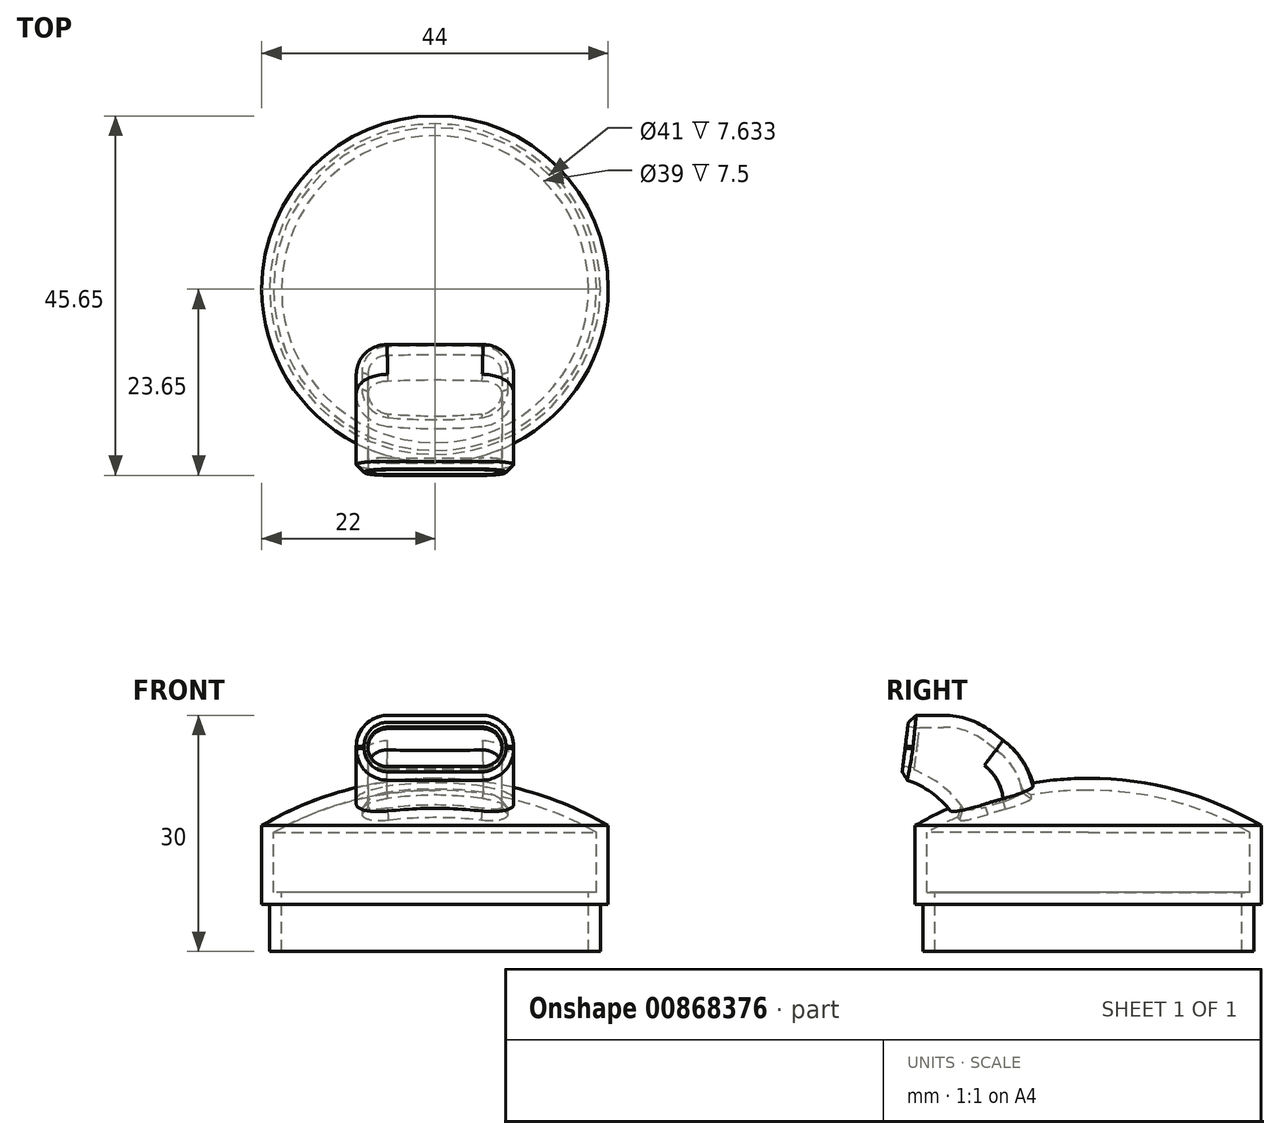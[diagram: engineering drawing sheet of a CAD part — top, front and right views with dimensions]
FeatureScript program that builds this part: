
annotation { "Feature Type Name" : "Feature", "Feature Type Description" : "" }
export const myFeature = defineFeature(function(context is Context, id is Id, definition is map)
    precondition{}
    {
        {
            var Q0;
            Q0=qCreatedBy(makeId("Front.planeOp"),FACE);
            var sketch = newSketch(context, id + "F0", { "sketchPlane" : qUnion([Q0])});
            skLineSegment(sketch, "E0", {"start": v(0, 0) * mm, "end": v(-21, 0) * mm});
            skLineSegment(sketch, "E1", {"start": v(-21, 0) * mm, "end": v(-21, 6) * mm});
            skLineSegment(sketch, "E2", {"start": v(-21, 6) * mm, "end": v(-22, 6) * mm});
            skLineSegment(sketch, "E3", {"start": v(-22, 6) * mm, "end": v(-22, 16) * mm});
            skLineSegment(sketch, "E4", {"start": v(0, 22) * mm, "end": v(0, 0) * mm});
            skArc(sketch, "E5", {"start": v(0, 22) * mm, "mid": v(-11.4, 20.47) * mm, "end": v(-22, 16) * mm});
            skSolve(sketch);
        }
        {
            var Q0;
            Q0 = qSketchRegion(id + "F0", true);
            var Q1;
            Q1=sQuery(id+"F0.wireOp",EDGE,"E4");
            revolve(context, id + "F1", {"surfaceOperationType" : NewSurfaceOperationType.NEW, "entities" : qUnion([Q0]), "axis" : qUnion([Q1]), "revolveType" : RevolveType.FULL});
        }
        {
            var Q0;
            Q0=qCreatedBy(makeId("Top.planeOp"),FACE);
            var sketch = newSketch(context, id + "F2", { "sketchPlane" : qUnion([Q0])});
            skLineSegment(sketch, "E6.bottom", {"start": v(-10, -7.05) * mm, "end": v(10, -7.05) * mm});
            skLineSegment(sketch, "E6.top", {"start": v(-10, -17.05) * mm, "end": v(10, -17.05) * mm});
            skLineSegment(sketch, "E6.left", {"start": v(-10, -7.05) * mm, "end": v(-10, -17.05) * mm});
            skLineSegment(sketch, "E6.right", {"start": v(10, -7.05) * mm, "end": v(10, -17.05) * mm});
            skSolve(sketch);
        }
        {
            var Q0;
            Q0 = qSketchRegion(id + "F2", true);
            extrude(context, id + "F3", {"entities" : qUnion([Q0]), "operationType" : NewBodyOperationType.ADD, "depth" : 30 * mm, "offsetDistance" : 25 * mm});
        }
        {
            var Q0;
            Q0=makeQuery(id+"F3.opExtrude","SWEPT_FACE",FACE,{"disambiguationData":[OSD([sQuery(id+"F2.wireOp",EDGE,"E6.right")])]});
            var sketch = newSketch(context, id + "F4", { "sketchPlane" : qUnion([Q0])});
            skLineSegment(sketch, "E7", {"start": v(-23.76, 22) * mm, "end": v(-23.76, 30) * mm});
            skLineSegment(sketch, "E8", {"start": v(-23.76, 30) * mm, "end": v(-17.05, 30) * mm});
            skLineSegment(sketch, "E9", {"start": v(-17.05, 30) * mm, "end": v(-17.05, 17.23) * mm});
            skArc(sketch, "E10", {"start": v(-17.05, 17.23) * mm, "mid": v(-19.97, 20.22) * mm, "end": v(-23.76, 22) * mm});
            skSolve(sketch);
        }
        {
            var Q0;
            Q0 = qSketchRegion(id + "F4", true);
            var Q1;
            Q1=makeQuery(id+"F3.opExtrude","SWEPT_FACE",FACE,{"disambiguationData":[OSD([sQuery(id+"F2.wireOp",EDGE,"E6.left")])]});
            extrude(context, id + "F5", {"entities" : qUnion([Q0]), "operationType" : NewBodyOperationType.ADD, "endBound" : BoundingType.UP_TO_SURFACE, "oppositeDirection" : true, "depth" : 25 * mm, "endBoundEntityFace" : qUnion([Q1]), "offsetDistance" : 25 * mm});
        }
        {
            var Q0;
            Q0=makeQuery(id+"F3.opExtrude","CAP_EDGE",EDGE,{"disambiguationData":[OSD([sQuery(id+"F2.wireOp",EDGE,"E6.bottom")])],"isStart":false});
            chamfer(context, id + "F6", {"entities" : qUnion([Q0]), "chamferType" : ChamferType.TWO_OFFSETS, "width1" : 6 * mm, "oppositeDirection" : false, "width2" : 8 * mm, "tangentPropagation" : true});
        }
        {
            var Q0;
            {var subQ0=sQuery(id+"F2.wireOp",EDGE,"E6.bottom");Q0=makeQuery(id+"F6.opChamfer","BLEND_EDGE",EDGE,{"blendedFrom":[makeQuery(id+"F3.opExtrude","CAP_EDGE",EDGE,{"disambiguationData":[OSD([subQ0])],"isStart":false}),makeQuery(id+"F5.boolean.opBoolean","MERGE",FACE,{"derivedFrom":[makeQuery(id+"F3.opExtrude","CAP_FACE",FACE,{"disambiguationData":[OSD([subQ0,sQuery(id+"F2.wireOp",EDGE,"E6.top"),sQuery(id+"F2.wireOp",EDGE,"E6.left"),sQuery(id+"F2.wireOp",EDGE,"E6.right")])],"isStart":false}),makeQuery(id+"F5.opExtrude","SWEPT_FACE",FACE,{"disambiguationData":[OSD([sQuery(id+"F4.wireOp",EDGE,"E8")])]})]})],"blendedInto":[makeQuery(id+"F5.boolean.opBoolean","MERGE",FACE,{"derivedFrom":[makeQuery(id+"F3.opExtrude","CAP_FACE",FACE,{"disambiguationData":[OSD([subQ0,sQuery(id+"F2.wireOp",EDGE,"E6.top"),sQuery(id+"F2.wireOp",EDGE,"E6.left"),sQuery(id+"F2.wireOp",EDGE,"E6.right")])],"isStart":false}),makeQuery(id+"F5.opExtrude","SWEPT_FACE",FACE,{"disambiguationData":[OSD([sQuery(id+"F4.wireOp",EDGE,"E8")])]})]})]});}
            var Q1;
            {var subQ0=sQuery(id+"F2.wireOp",EDGE,"E6.bottom");Q1=makeQuery(id+"F6.opChamfer","BLEND_EDGE",EDGE,{"blendedFrom":[makeQuery(id+"F3.opExtrude","CAP_EDGE",EDGE,{"disambiguationData":[OSD([subQ0])],"isStart":false}),makeQuery(id+"F3.opExtrude","SWEPT_FACE",FACE,{"disambiguationData":[OSD([subQ0])]})],"blendedInto":[makeQuery(id+"F3.opExtrude","SWEPT_FACE",FACE,{"disambiguationData":[OSD([subQ0])]})]});}
            fillet(context, id + "F7", {"entities" : qUnion([Q0, Q1]), "radius" : 10 * mm, "tangentPropagation" : true, "allowEdgeOverflow" : false});
        }
        {
            var Q0;
            Q0=makeQuery(id+"F5.opExtrude","SWEPT_EDGE",EDGE,{"disambiguationData":[OSD([sQuery(id+"F4.wireOp",EDGE,"E7"),sQuery(id+"F4.wireOp",EDGE,"E8")])]});
            chamfer(context, id + "F8", {"entities" : qUnion([Q0]), "chamferType" : ChamferType.TWO_OFFSETS, "width1" : 1 * mm, "oppositeDirection" : false, "width2" : 8 * mm, "tangentPropagation" : true});
        }
        {
            var Q0;
            Q0=makeQuery(id+"F5.opExtrude","CAP_EDGE",EDGE,{"disambiguationData":[OSD([sQuery(id+"F4.wireOp",EDGE,"E10")])],"isStart":true});
            var Q1;
            Q1=makeQuery(id+"F5.boolean.opBoolean","MERGE",EDGE,{"derivedFrom":[makeQuery(id+"F3.opExtrude","CAP_EDGE",EDGE,{"disambiguationData":[OSD([sQuery(id+"F2.wireOp",EDGE,"E6.right")])],"isStart":false}),makeQuery(id+"F5.opExtrude","CAP_EDGE",EDGE,{"disambiguationData":[OSD([sQuery(id+"F4.wireOp",EDGE,"E8")])],"isStart":true})]});
            var Q2;
            Q2=makeQuery(id+"F5.opExtrude","CAP_EDGE",EDGE,{"disambiguationData":[OSD([sQuery(id+"F4.wireOp",EDGE,"E10")])],"isStart":false});
            var Q3;
            Q3=makeQuery(id+"F5.boolean.opBoolean","MERGE",EDGE,{"derivedFrom":[makeQuery(id+"F3.opExtrude","CAP_EDGE",EDGE,{"disambiguationData":[OSD([sQuery(id+"F2.wireOp",EDGE,"E6.left")])],"isStart":false}),makeQuery(id+"F5.opExtrude","CAP_EDGE",EDGE,{"disambiguationData":[OSD([sQuery(id+"F4.wireOp",EDGE,"E8")])],"isStart":false})]});
            fillet(context, id + "F9", {"entities" : qUnion([Q0, Q1, Q2, Q3]), "radius" : 4 * mm, "tangentPropagation" : true, "allowEdgeOverflow" : false});
        }
        {
            var Q0;
            Q0=makeQuery(id+"F1.opRevolve","SWEPT_FACE",FACE,{"disambiguationData":[OSD([sQuery(id+"F0.wireOp",EDGE,"E0")])]});
            shell(context, id + "F10", {"entities" : qUnion([Q0]), "thickness" : 1.5 * mm});
        }
        {
            var Q0;
            Q0=makeQuery(id+"F8.opChamfer","BLEND_FACE",FACE,{"disambiguationData":[OSD([sQuery(id+"F4.wireOp",EDGE,"E7"),sQuery(id+"F4.wireOp",EDGE,"E8")])]});
            var sketch = newSketch(context, id + "F11", { "sketchPlane" : qUnion([Q0])});
            skLineSegment(sketch, "E11", {"start": v(-6, 25.45) * mm, "end": v(6, 25.45) * mm});
            skLineSegment(sketch, "E12", {"start": v(-6, 20.38) * mm, "end": v(6, 20.38) * mm});
            skArc(sketch, "E13", {"start": v(-6, 20.38) * mm, "mid": v(-8.53, 22.91) * mm, "end": v(-6, 25.45) * mm});
            skArc(sketch, "E14", {"start": v(6, 25.45) * mm, "mid": v(8.53, 22.91) * mm, "end": v(6, 20.38) * mm});
            skLineSegment(sketch, "E15", {"start": v(-6, 25.45) * mm, "end": v(-6, 26.95) * mm, "construction": true});
            skSolve(sketch);
        }
        {
            var Q0;
            Q0 = qSketchRegion(id + "F11", true);
            extrude(context, id + "F12", {"entities" : qUnion([Q0]), "operationType" : NewBodyOperationType.REMOVE, "oppositeDirection" : true, "depth" : 1.5 * mm, "offsetDistance" : 25 * mm});
        }
        {
            var Q0;
            {var subQ0=sQuery(id+"F4.wireOp",EDGE,"E10");var subQ1=sQuery(id+"F0.wireOp",EDGE,"E5");Q0=makeQuery(id+"F10.opShell","OFFSET_EDGE",EDGE,{"disambiguationData":[OSD([subQ1,subQ0]),TDD([makeQuery(id+"F5.boolean.opBoolean","INTERSECT",EDGE,{"derivedFrom":[makeQuery(id+"F1.opRevolve","SWEPT_FACE",FACE,{"disambiguationData":[OSD([subQ1])]}),makeQuery(id+"F5.opExtrude","SWEPT_FACE",FACE,{"disambiguationData":[OSD([subQ0])]})]})])]});}
            chamfer(context, id + "F13", {"entities" : qUnion([Q0]), "width" : 1 * mm, "tangentPropagation" : true});
        }
        {
            var Q0;
            {var subQ0=sQuery(id+"F4.wireOp",EDGE,"E8");Q0=makeQuery(id+"F9.opFillet","BLEND_EDGE",EDGE,{"blendedFrom":[makeQuery(id+"F5.boolean.opBoolean","MERGE",EDGE,{"derivedFrom":[makeQuery(id+"F3.opExtrude","CAP_EDGE",EDGE,{"disambiguationData":[OSD([sQuery(id+"F2.wireOp",EDGE,"E6.right")])],"isStart":false}),makeQuery(id+"F5.opExtrude","CAP_EDGE",EDGE,{"disambiguationData":[OSD([subQ0])],"isStart":true})]}),makeQuery(id+"F8.opChamfer","BLEND_FACE",FACE,{"disambiguationData":[OSD([sQuery(id+"F4.wireOp",EDGE,"E7"),subQ0])]})],"blendedInto":[makeQuery(id+"F8.opChamfer","BLEND_FACE",FACE,{"disambiguationData":[OSD([sQuery(id+"F4.wireOp",EDGE,"E7"),subQ0])]})]});}
            chamfer(context, id + "F14", {"entities" : qUnion([Q0]), "width" : 1 * mm, "tangentPropagation" : true});
        }
    });
